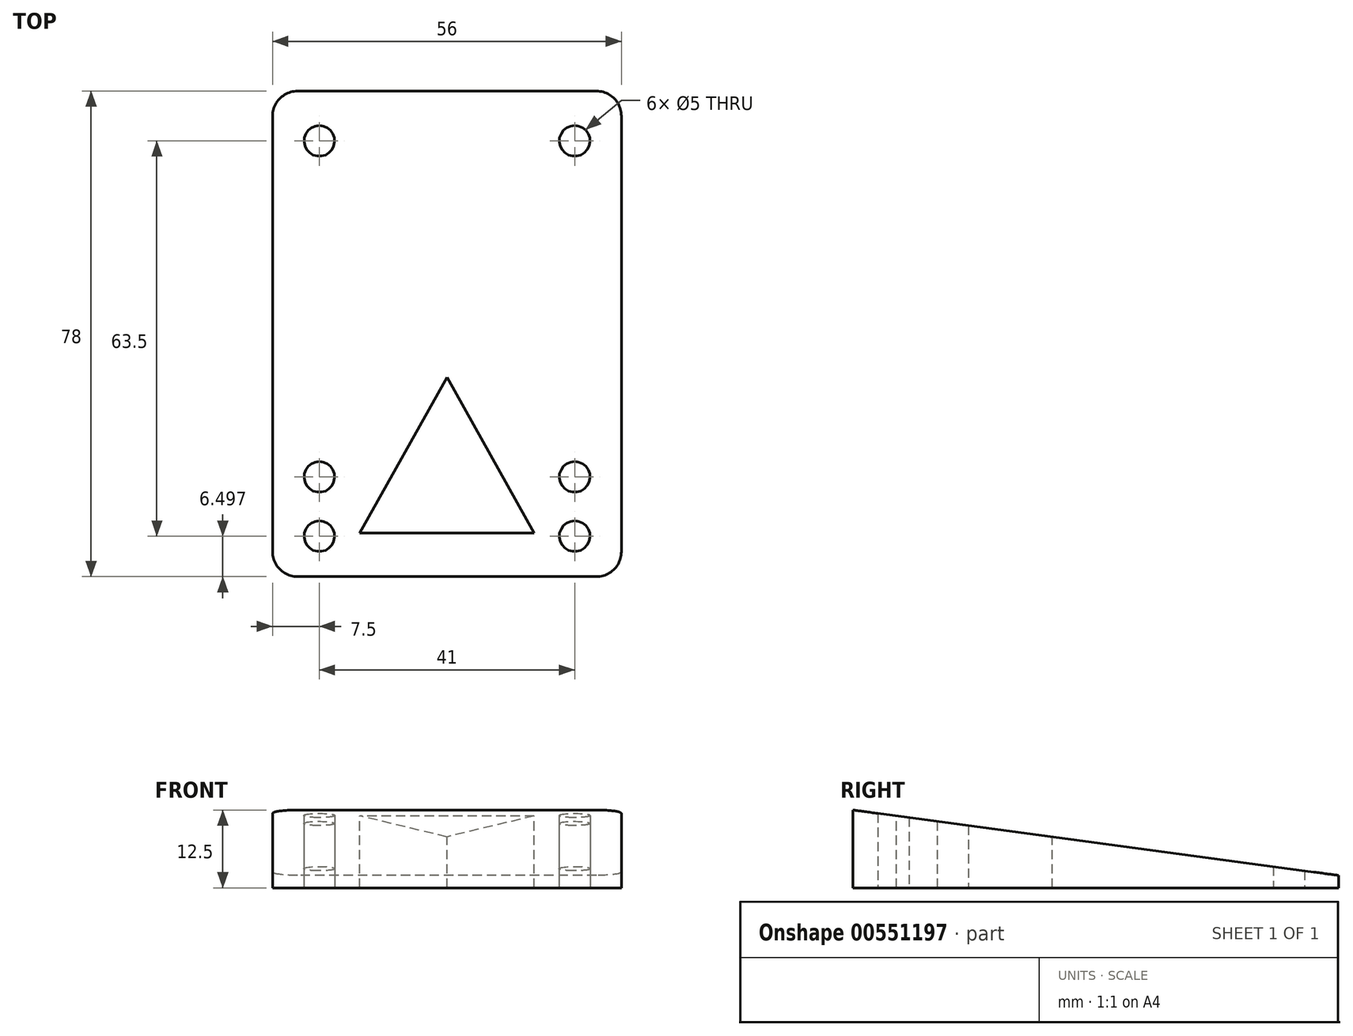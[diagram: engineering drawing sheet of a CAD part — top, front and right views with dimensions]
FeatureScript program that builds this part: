
annotation { "Feature Type Name" : "Feature", "Feature Type Description" : "" }
export const myFeature = defineFeature(function(context is Context, id is Id, definition is map)
    precondition{}
    {
        {
            var Q0;
            Q0=qCreatedBy(makeId("Top.planeOp"),FACE);
            var sketch = newSketch(context, id + "F0", { "sketchPlane" : qUnion([Q0])});
            skLineSegment(sketch, "E0.bottom", {"start": v(-18.85, 36.64) * mm, "end": v(29.15, 36.64) * mm});
            skLineSegment(sketch, "E0.top", {"start": v(-18.85, -41.36) * mm, "end": v(29.15, -41.36) * mm});
            skLineSegment(sketch, "E0.left", {"start": v(-22.85, 32.64) * mm, "end": v(-22.85, -37.36) * mm});
            skLineSegment(sketch, "E0.right", {"start": v(33.15, 32.64) * mm, "end": v(33.15, -37.36) * mm});
            skCircle(sketch, "E1", {"center": v(-15.35, 28.64) * mm, "radius": 2.5 * mm});
            skCircle(sketch, "E2", {"center": v(25.65, 28.64) * mm, "radius": 2.5 * mm});
            skCircle(sketch, "E3", {"center": v(-15.35, -34.86) * mm, "radius": 2.5 * mm});
            skCircle(sketch, "E4", {"center": v(25.65, -34.86) * mm, "radius": 2.5 * mm});
            skPoint(sketch, "E5.visualSharp", {"position": v(-22.85, 36.64) * mm});
            skArc(sketch, "E5.filletArc", {"start": v(-18.85, 36.64) * mm, "mid": v(-21.68, 35.47) * mm, "end": v(-22.85, 32.64) * mm});
            skPoint(sketch, "E6.visualSharp", {"position": v(33.15, 36.64) * mm});
            skArc(sketch, "E6.filletArc", {"start": v(33.15, 32.64) * mm, "mid": v(31.98, 35.47) * mm, "end": v(29.15, 36.64) * mm});
            skPoint(sketch, "E7.visualSharp", {"position": v(33.15, -41.36) * mm});
            skArc(sketch, "E7.filletArc", {"start": v(29.15, -41.36) * mm, "mid": v(31.98, -40.2) * mm, "end": v(33.15, -37.36) * mm});
            skPoint(sketch, "E8.visualSharp", {"position": v(-22.85, -41.36) * mm});
            skArc(sketch, "E8.filletArc", {"start": v(-22.85, -37.36) * mm, "mid": v(-21.68, -40.2) * mm, "end": v(-18.85, -41.36) * mm});
            skCircle(sketch, "E9", {"center": v(25.65, -25.34) * mm, "radius": 2.5 * mm});
            skCircle(sketch, "E10", {"center": v(-15.35, -25.34) * mm, "radius": 2.5 * mm});
            skSolve(sketch);
        }
        {
            var Q0;
            Q0=makeQuery(id+"F0.imprint","IMPRINT",FACE,{"disambiguationData":[TD([[makeQuery(id+"F0.imprint","IMPRINT",EDGE,{"derivedFrom":sQuery(id+"F0.wireOp",EDGE,"E0.bottom")}),-1.0]])]});
            extrude(context, id + "F1", {"entities" : qUnion([Q0]), "depth" : 20 * mm, "offsetDistance" : 25 * mm});
        }
        {
            var Q0;
            Q0=makeQuery(id+"F1.opExtrude","CAP_FACE",FACE,{"disambiguationData":[OSD([sQuery(id+"F0.wireOp",EDGE,"E0.bottom"),sQuery(id+"F0.wireOp",EDGE,"E0.top"),sQuery(id+"F0.wireOp",EDGE,"E0.left"),sQuery(id+"F0.wireOp",EDGE,"E0.right"),sQuery(id+"F0.wireOp",EDGE,"E1"),sQuery(id+"F0.wireOp",EDGE,"E2"),sQuery(id+"F0.wireOp",EDGE,"E3"),sQuery(id+"F0.wireOp",EDGE,"E4"),sQuery(id+"F0.wireOp",EDGE,"E5.filletArc"),sQuery(id+"F0.wireOp",EDGE,"E6.filletArc"),sQuery(id+"F0.wireOp",EDGE,"E7.filletArc"),sQuery(id+"F0.wireOp",EDGE,"E8.filletArc")])],"isStart":false});
            var sketch = newSketch(context, id + "F2", { "sketchPlane" : qUnion([Q0])});
            skLineSegment(sketch, "E11", {"start": v(-8.85, 31.64) * mm, "end": v(19.15, 31.64) * mm});
            skLineSegment(sketch, "E12", {"start": v(19.15, 31.64) * mm, "end": v(5.15, 6.64) * mm});
            skPoint(sketch, "E12.endSnap0", {"position": v(5.15, 31.64) * mm});
            skLineSegment(sketch, "E13", {"start": v(-8.85, 31.64) * mm, "end": v(5.15, 6.64) * mm});
            skLineSegment(sketch, "E14", {"start": v(-8.85, -34.36) * mm, "end": v(19.15, -34.36) * mm});
            skLineSegment(sketch, "E15", {"start": v(-8.85, -34.36) * mm, "end": v(5.15, -9.36) * mm});
            skLineSegment(sketch, "E16", {"start": v(5.15, -9.36) * mm, "end": v(19.15, -34.36) * mm});
            skLineSegment(sketch, "E17", {"start": v(-16.85, 23.91) * mm, "end": v(-9.85, 23.91) * mm});
            skLineSegment(sketch, "E18", {"start": v(-9.85, 23.91) * mm, "end": v(-0.85, 8.91) * mm});
            skLineSegment(sketch, "E19", {"start": v(-16.85, 23.91) * mm, "end": v(-16.85, 6.91) * mm});
            skLineSegment(sketch, "E20", {"start": v(-16.85, 6.91) * mm, "end": v(-0.85, 6.91) * mm});
            skLineSegment(sketch, "E21", {"start": v(-0.85, 8.91) * mm, "end": v(-0.85, 6.91) * mm});
            skSolve(sketch);
        }
        {
            var Q0;
            Q0=makeQuery(id+"F2.imprint","IMPRINT",FACE,{"disambiguationData":[TD([[makeQuery(id+"F2.imprint","IMPRINT",EDGE,{"derivedFrom":sQuery(id+"F2.wireOp",EDGE,"E14")}),1.0]])]});
            extrude(context, id + "F3", {"entities" : qUnion([Q0]), "operationType" : NewBodyOperationType.REMOVE, "oppositeDirection" : true, "depth" : 25 * mm});
        }
        {
            var Q0;
            Q0=qCreatedBy(makeId("Right.planeOp"),FACE);
            var sketch = newSketch(context, id + "F4", { "sketchPlane" : qUnion([Q0])});
            skLineSegment(sketch, "E22", {"start": v(36.64, 20) * mm, "end": v(-41.36, 20) * mm});
            skLineSegment(sketch, "E23", {"start": v(-41.36, 12.5) * mm, "end": v(36.64, 2) * mm});
            skLineSegment(sketch, "E24", {"start": v(36.64, 2) * mm, "end": v(36.64, 20) * mm});
            skLineSegment(sketch, "E25", {"start": v(-41.36, 0) * mm, "end": v(-41.36, 20) * mm, "construction": true});
            skLineSegment(sketch, "E26", {"start": v(36.64, 0) * mm, "end": v(36.64, 20) * mm, "construction": true});
            skLineSegment(sketch, "E27", {"start": v(-41.36, 20) * mm, "end": v(-41.36, 12.5) * mm});
            skSolve(sketch);
        }
        {
            var Q0;
            Q0=qSketchRegion(id+"F4",true);
            extrude(context, id + "F5", {"entities" : qUnion([Q0]), "operationType" : NewBodyOperationType.REMOVE, "endBound" : BoundingType.THROUGH_ALL, "depth" : 25 * mm, "offsetDistance" : 25 * mm, "hasSecondDirection" : true, "secondDirectionBound" : SecondDirectionBoundingType.THROUGH_ALL, "secondDirectionOppositeDirection" : true, "secondDirectionDepth" : 25 * mm});
        }
    });
